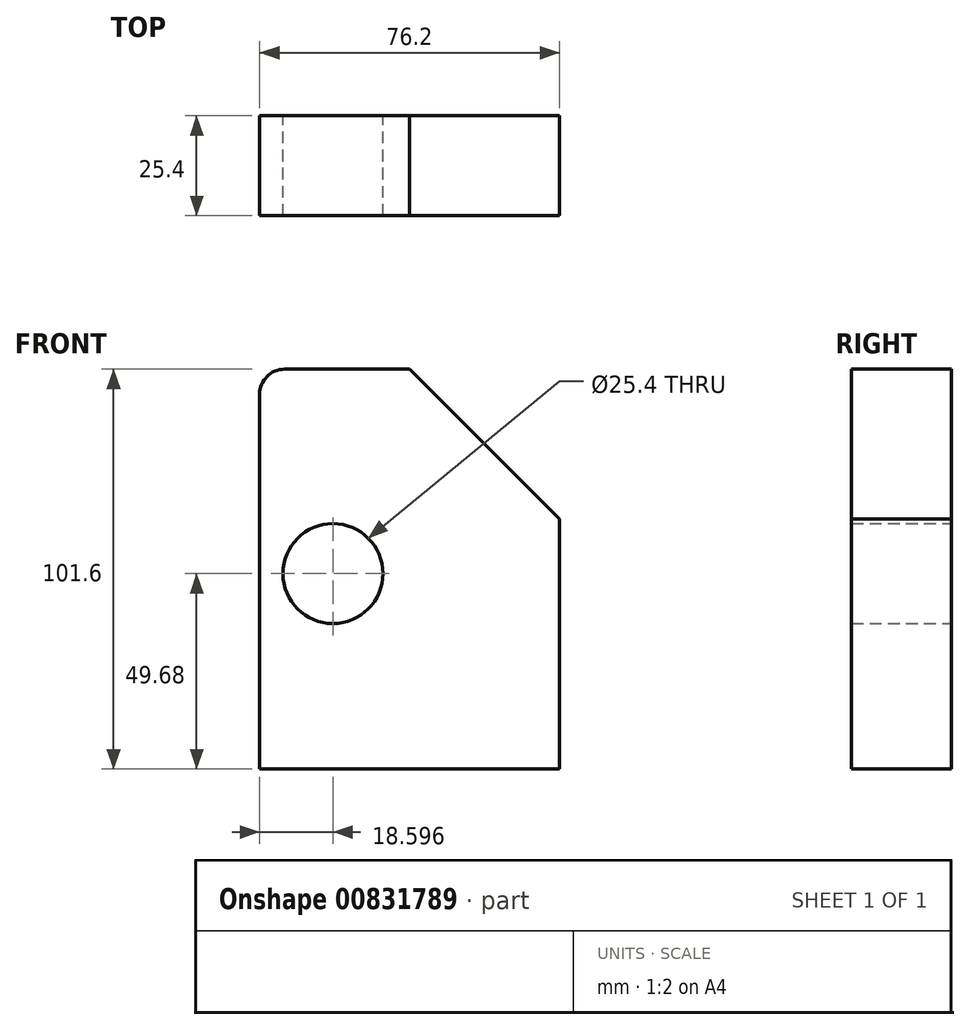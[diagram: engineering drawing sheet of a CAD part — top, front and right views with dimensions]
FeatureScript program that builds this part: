
annotation { "Feature Type Name" : "Feature", "Feature Type Description" : "" }
export const myFeature = defineFeature(function(context is Context, id is Id, definition is map)
    precondition{}
    {
        {
            var Q0;
            Q0=qCreatedBy(makeId("Front.planeOp"),FACE);
            var sketch = newSketch(context, id + "F0", { "sketchPlane" : qUnion([Q0])});
            skLineSegment(sketch, "E0.bottom", {"start": v(-77.14, 51.92) * mm, "end": v(-0.94, 51.92) * mm});
            skLineSegment(sketch, "E0.top", {"start": v(-77.14, -49.68) * mm, "end": v(-0.94, -49.68) * mm});
            skLineSegment(sketch, "E0.left", {"start": v(-77.14, 51.92) * mm, "end": v(-77.14, -49.68) * mm});
            skLineSegment(sketch, "E0.right", {"start": v(-0.94, 51.92) * mm, "end": v(-0.94, -49.68) * mm});
            skCircle(sketch, "E1", {"center": v(-58.54, 0) * mm, "radius": 12.7 * mm});
            skSolve(sketch);
        }
        {
            var Q0;
            Q0=makeQuery(id+"F0.imprint","IMPRINT",FACE,{"disambiguationData":[TD([[makeQuery(id+"F0.imprint","IMPRINT",EDGE,{"derivedFrom":sQuery(id+"F0.wireOp",EDGE,"E0.bottom")}),-1.0]])]});
            extrude(context, id + "F1", {"entities" : qUnion([Q0]), "depth" : 25.4 * mm, "offsetDistance" : 25.4 * mm});
        }
        {
            var Q0;
            Q0=makeQuery(id+"F1.opExtrude","SWEPT_EDGE",EDGE,{"disambiguationData":[OSD([sQuery(id+"F0.wireOp",EDGE,"E0.bottom"),sQuery(id+"F0.wireOp",EDGE,"E0.right")])]});
            chamfer(context, id + "F2", {"entities" : qUnion([Q0]), "width" : 38.1 * mm, "tangentPropagation" : true});
        }
        {
            var Q0;
            Q0=makeQuery(id+"F1.opExtrude","SWEPT_EDGE",EDGE,{"disambiguationData":[OSD([sQuery(id+"F0.wireOp",EDGE,"E0.bottom"),sQuery(id+"F0.wireOp",EDGE,"E0.left")])]});
            fillet(context, id + "F3", {"entities" : qUnion([Q0]), "radius" : 6.35 * mm, "tangentPropagation" : true, "allowEdgeOverflow" : false});
        }
    });
